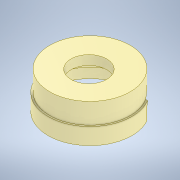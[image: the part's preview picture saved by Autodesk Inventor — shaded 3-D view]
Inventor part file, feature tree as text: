
AUTODESK INVENTOR PART (.ipt)
format: ipt  version: 2022 (Build 260153000, 153)  size: 209,408 bytes
history: native  units: mm
features: sketch x7, extrude x7, revolve x1
ambient origin geometry x8: Origin, YZ Plane, XZ Plane, XY Plane, X Axis, Y Axis, Z Axis, Center Point
bodies: Solid1 (feature_tree)
feature tree (15):
  revolve  "Revolution1"  [1 undecoded]
  sketch  "Sketch5"  dims[d2=16.2mm d3=2.0mm]
  extrude  "Extrusion2"  Depth=2.0mm
  extrude  "Extrusion3"  Depth=1.5mm
  extrude  "Extrusion5"  Depth=2.5mm
  extrude  "Extrusion6"  Depth=1.0mm
  extrude  "Extrusion4"  Depth=73.0mm
  extrude  "Extrusion7"  Depth=10.0mm TaperAngle=0.0deg
  extrude  "Extrusion8"  Depth=10.0mm
  sketch  "Sketch1"  dims[d0=6.55mm d1=14.6mm]
  sketch  "Sketch6"  dims[d4=8.5mm d5=1.5mm]
  sketch  "Sketch7"  dims[d6=3.0mm d7=2.5mm]
  sketch  "Sketch8"  dims[d8=360.0deg d29=1.0mm]
  sketch  "Sketch9"  dims[d30=70.0mm d31=73.0mm]
  sketch  "Sketch10"  dims[d32=3.0mm d33=0.0mm d34=23.7mm d35=0.0mm d36=19.5mm d37=7.5mm d38=15.5mm d39=0.0mm d40=0.0mm d41=10.0mm d42=0.0mm d43=73.0mm d44=1.0mm d45=76.0mm d46=10.0mm d47=0.0mm d48=0.0mm d49=0.0mm d50=5.0mm d51=0.0mm d55=0.0mm d56=0.0mm d57=20.5mm d58=7.5mm d59=18.0mm]
note: 1 required parameter value undecoded (feature->parameter linkage not recoverable at this tier; creation-order binding heuristic only, values carry confidence <= 0.55)
